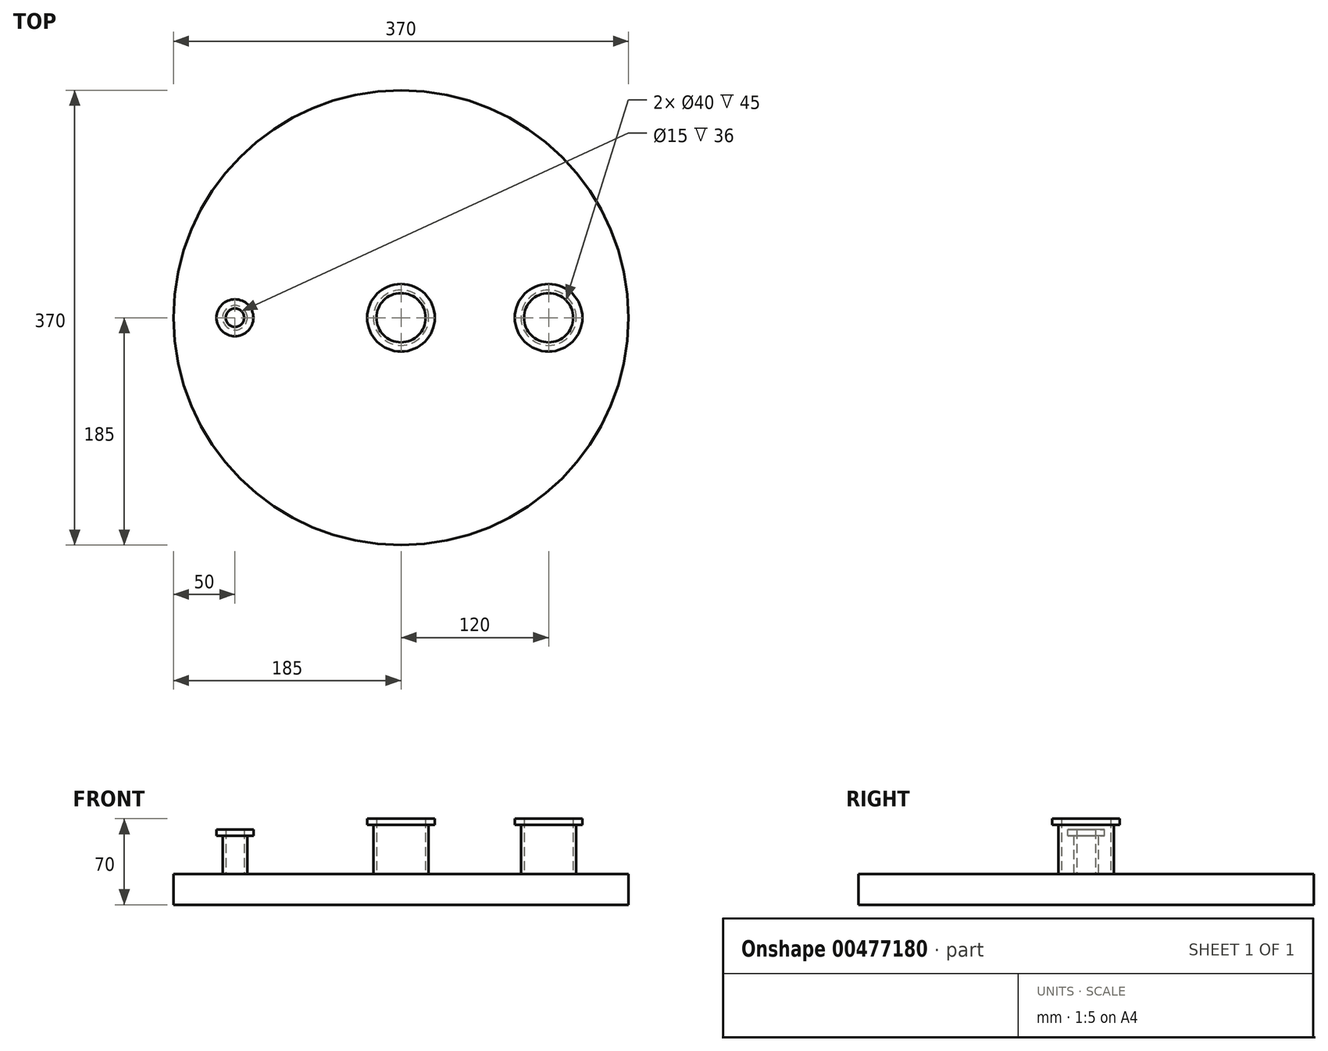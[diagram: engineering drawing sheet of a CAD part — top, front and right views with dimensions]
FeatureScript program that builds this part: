
annotation { "Feature Type Name" : "Feature", "Feature Type Description" : "" }
export const myFeature = defineFeature(function(context is Context, id is Id, definition is map)
    precondition{}
    {
        {
            var Q0;
            Q0=qCreatedBy(makeId("Top.planeOp"),FACE);
            var sketch = newSketch(context, id + "F0", { "sketchPlane" : qUnion([Q0])});
            skCircle(sketch, "E0", {"center": v(0, 0) * mm, "radius": 185 * mm});
            skSolve(sketch);
        }
        {
            var Q0;
            Q0 = qSketchRegion(id + "F0", true);
            extrude(context, id + "F1", {"entities" : qUnion([Q0]), "depth" : 25 * mm});
        }
        {
            var Q0;
            Q0=makeQuery(id+"F1.opExtrude","CAP_FACE",FACE,{"disambiguationData":[OSD([sQuery(id+"F0.wireOp",EDGE,"E0")])],"isStart":false});
            var sketch = newSketch(context, id + "F2", { "sketchPlane" : qUnion([Q0])});
            skCircle(sketch, "E1", {"center": v(0, 0) * mm, "radius": 20 * mm});
            skCircle(sketch, "E2", {"center": v(-135, 0) * mm, "radius": 7.5 * mm});
            skCircle(sketch, "E3", {"center": v(120, 0) * mm, "radius": 20 * mm});
            skCircle(sketch, "E4", {"center": v(120, 0) * mm, "radius": 22.5 * mm});
            skCircle(sketch, "E5", {"center": v(0, 0) * mm, "radius": 22.5 * mm});
            skCircle(sketch, "E6", {"center": v(-135, 0) * mm, "radius": 10 * mm});
            skSolve(sketch);
        }
        {
            var Q0;
            Q0=makeQuery(id+"F2.imprint","IMPRINT",FACE,{"disambiguationData":[TD([[makeQuery(id+"F2.imprint","IMPRINT",EDGE,{"derivedFrom":sQuery(id+"F2.wireOp",EDGE,"E1")}),-1.0]])]});
            var Q1;
            Q1=makeQuery(id+"F2.imprint","IMPRINT",FACE,{"disambiguationData":[TD([[makeQuery(id+"F2.imprint","IMPRINT",EDGE,{"derivedFrom":sQuery(id+"F2.wireOp",EDGE,"E3")}),-1.0]])]});
            extrude(context, id + "F3", {"entities" : qUnion([Q0, Q1]), "operationType" : NewBodyOperationType.ADD, "depth" : 40 * mm});
        }
        {
            var Q0;
            Q0 = qSketchRegion(id + "F2", true);
            extrude(context, id + "F4", {"entities" : qUnion([Q0]), "operationType" : NewBodyOperationType.ADD, "depth" : 36 * mm});
        }
        {
            var Q0;
            Q0=makeQuery(id+"F3.opExtrude","CAP_FACE",FACE,{"disambiguationData":[OSD([sQuery(id+"F2.wireOp",EDGE,"E1"),sQuery(id+"F2.wireOp",EDGE,"E5")])],"isStart":false});
            var Q1;
            Q1=makeQuery(id+"F3.opExtrude","CAP_FACE",FACE,{"disambiguationData":[OSD([sQuery(id+"F2.wireOp",EDGE,"E3"),sQuery(id+"F2.wireOp",EDGE,"E4")])],"isStart":false});
            extrude(context, id + "F5", {"entities" : qUnion([Q0, Q1]), "operationType" : NewBodyOperationType.ADD, "depth" : (41 - 36) * mm});
        }
        {
            var Q0;
            Q0=makeQuery(id+"F5.opExtrude","CAP_FACE",FACE,{"disambiguationData":[OSD([sQuery(id+"F2.wireOp",EDGE,"E3"),sQuery(id+"F2.wireOp",EDGE,"E4")])],"isStart":false});
            var sketch = newSketch(context, id + "F6", { "sketchPlane" : qUnion([Q0])});
            skCircle(sketch, "E7", {"center": v(120, 0) * mm, "radius": 27.5 * mm});
            skCircle(sketch, "E8", {"center": v(0, 0) * mm, "radius": 27.5 * mm});
            skCircle(sketch, "E9", {"center": v(0, 0) * mm, "radius": 20 * mm});
            skCircle(sketch, "E10", {"center": v(120, 0) * mm, "radius": 20 * mm});
            skSolve(sketch);
        }
        {
            var Q0;
            Q0 = qSketchRegion(id + "F6", true);
            extrude(context, id + "F7", {"entities" : qUnion([Q0]), "operationType" : NewBodyOperationType.ADD, "oppositeDirection" : true, "depth" : 5 * mm});
        }
        {
            var Q0;
            Q0=makeQuery(id+"F4.opExtrude","CAP_FACE",FACE,{"disambiguationData":[OSD([sQuery(id+"F2.wireOp",EDGE,"E2"),sQuery(id+"F2.wireOp",EDGE,"E6")])],"isStart":false});
            var sketch = newSketch(context, id + "F8", { "sketchPlane" : qUnion([Q0])});
            skCircle(sketch, "E11", {"center": v(-135, 0) * mm, "radius": 7.5 * mm});
            skCircle(sketch, "E12", {"center": v(-135, 0) * mm, "radius": 15 * mm});
            skSolve(sketch);
        }
        {
            var Q0;
            Q0 = qSketchRegion(id + "F8", true);
            extrude(context, id + "F9", {"entities" : qUnion([Q0]), "operationType" : NewBodyOperationType.ADD, "oppositeDirection" : true, "depth" : 5 * mm});
        }
    });
